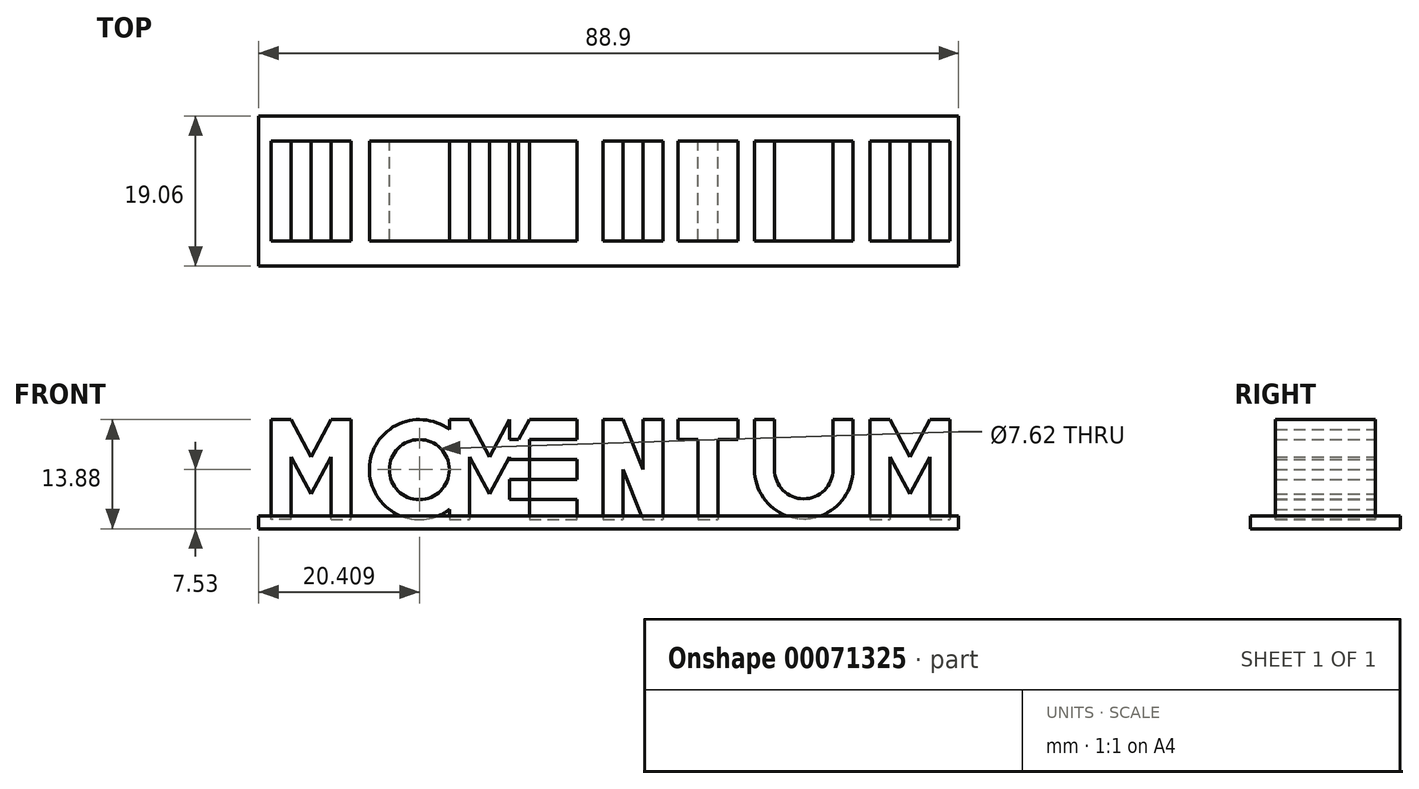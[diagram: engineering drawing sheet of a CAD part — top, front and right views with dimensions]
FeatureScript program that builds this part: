
annotation { "Feature Type Name" : "Feature", "Feature Type Description" : "" }
export const myFeature = defineFeature(function(context is Context, id is Id, definition is map)
    precondition{}
    {
        {
            var Q0;
            Q0=qCreatedBy(makeId("Front.planeOp"),FACE);
            var sketch = newSketch(context, id + "F0", { "sketchPlane" : qUnion([Q0])});
            skLineSegment(sketch, "E0.rect.bottom", {"start": v(-39.63, -6.35) * mm, "end": v(-42.17, -6.35) * mm});
            skLineSegment(sketch, "E0.rect.top", {"start": v(-39.63, 6.35) * mm, "end": v(-42.17, 6.35) * mm});
            skLineSegment(sketch, "E0.rect.left", {"start": v(-39.63, -6.35) * mm, "end": v(-39.63, 6.35) * mm});
            skLineSegment(sketch, "E0.rect.right", {"start": v(-42.17, -6.35) * mm, "end": v(-42.17, 6.35) * mm});
            skPoint(sketch, "E0.rect.middle", {"position": v(-40.9, 0) * mm});
            skLineSegment(sketch, "E1", {"start": v(-42.17, 6.35) * mm, "end": v(3.15, 6.35) * mm});
            skPoint(sketch, "E1.endSnap0", {"position": v(-40.9, 6.35) * mm});
            skLineSegment(sketch, "E2", {"start": v(-42.17, -6.35) * mm, "end": v(48.91, -6.35) * mm});
            skPoint(sketch, "E2.endSnap0", {"position": v(-40.9, -6.35) * mm});
            skLineSegment(sketch, "E3", {"start": v(-37.1, 6.35) * mm, "end": v(-37.1, -6.35) * mm});
            skLineSegment(sketch, "E4.MirrorCS", {"start": v(-34.55, -6.35) * mm, "end": v(-34.55, 6.35) * mm});
            skLineSegment(sketch, "E5.MirrorCS", {"start": v(-32.01, -6.35) * mm, "end": v(-32.01, 6.35) * mm});
            skLineSegment(sketch, "E6", {"start": v(-42.17, 6.35) * mm, "end": v(-37.1, -3.1) * mm});
            skLineSegment(sketch, "E7", {"start": v(-39.63, 6.35) * mm, "end": v(-37.1, 1.63) * mm});
            skLineSegment(sketch, "E8", {"start": v(-37.1, 1.63) * mm, "end": v(-34.55, 6.35) * mm});
            skLineSegment(sketch, "E9", {"start": v(-32.01, 6.35) * mm, "end": v(-37.1, -3.1) * mm});
            skCircle(sketch, "E10", {"center": v(-23.32, 0) * mm, "radius": 6.35 * mm});
            skCircle(sketch, "E11", {"center": v(-23.32, 0) * mm, "radius": 3.8 * mm});
            skLineSegment(sketch, "E12", {"start": v(-19.51, 0) * mm, "end": v(-16.97, 0) * mm});
            skLineSegment(sketch, "E13", {"start": v(-19.51, 6.35) * mm, "end": v(-19.51, -6.35) * mm});
            skLineSegment(sketch, "E14", {"start": v(-16.97, 6.35) * mm, "end": v(-16.97, -6.35) * mm});
            skLineSegment(sketch, "E15", {"start": v(-14.43, 6.35) * mm, "end": v(-14.43, -6.35) * mm});
            skLineSegment(sketch, "E16", {"start": v(-11.9, 6.35) * mm, "end": v(-11.9, -6.35) * mm});
            skLineSegment(sketch, "E17", {"start": v(-9.35, 6.35) * mm, "end": v(-9.35, -6.35) * mm});
            skLineSegment(sketch, "E18", {"start": v(-19.51, 6.35) * mm, "end": v(-14.43, -3.1) * mm});
            skLineSegment(sketch, "E19", {"start": v(-14.43, -3.1) * mm, "end": v(-9.35, 6.35) * mm});
            skLineSegment(sketch, "E20", {"start": v(-16.97, 6.35) * mm, "end": v(-14.43, 1.62) * mm});
            skLineSegment(sketch, "E21", {"start": v(-14.43, 1.62) * mm, "end": v(-11.9, 6.35) * mm});
            skLineSegment(sketch, "E22", {"start": v(3.15, 6.35) * mm, "end": v(48.32, 6.35) * mm});
            skLineSegment(sketch, "E23.bottom", {"start": v(-11.9, 6.35) * mm, "end": v(-3.3, 6.35) * mm});
            skLineSegment(sketch, "E23.top", {"start": v(-11.9, 3.81) * mm, "end": v(-3.3, 3.81) * mm});
            skLineSegment(sketch, "E23.left", {"start": v(-11.9, 6.35) * mm, "end": v(-11.9, 3.81) * mm});
            skLineSegment(sketch, "E23.right", {"start": v(-3.3, 6.35) * mm, "end": v(-3.3, 3.81) * mm});
            skLineSegment(sketch, "E24.bottom", {"start": v(-11.9, 1.27) * mm, "end": v(-3.3, 1.27) * mm});
            skLineSegment(sketch, "E24.top", {"start": v(-11.9, -1.27) * mm, "end": v(-3.3, -1.27) * mm});
            skLineSegment(sketch, "E24.left", {"start": v(-11.9, 1.27) * mm, "end": v(-11.9, -1.27) * mm});
            skLineSegment(sketch, "E24.right", {"start": v(-3.3, 1.27) * mm, "end": v(-3.3, -1.27) * mm});
            skLineSegment(sketch, "E25.bottom", {"start": v(-11.9, -6.35) * mm, "end": v(-3.3, -6.35) * mm});
            skLineSegment(sketch, "E25.top", {"start": v(-11.9, -3.8) * mm, "end": v(-3.3, -3.8) * mm});
            skLineSegment(sketch, "E25.left", {"start": v(-11.9, -6.35) * mm, "end": v(-11.9, -3.8) * mm});
            skLineSegment(sketch, "E25.right", {"start": v(-3.3, -6.35) * mm, "end": v(-3.3, -3.8) * mm});
            skLineSegment(sketch, "E26", {"start": v(0, 6.35) * mm, "end": v(0, -6.35) * mm});
            skLineSegment(sketch, "E27", {"start": v(2.54, 6.35) * mm, "end": v(2.54, -6.35) * mm});
            skLineSegment(sketch, "E28", {"start": v(5.08, 6.35) * mm, "end": v(5.08, -6.35) * mm});
            skLineSegment(sketch, "E29", {"start": v(7.62, 6.35) * mm, "end": v(7.62, -6.35) * mm});
            skLineSegment(sketch, "E30", {"start": v(0, 6.35) * mm, "end": v(5.08, -6.35) * mm});
            skLineSegment(sketch, "E31", {"start": v(2.54, 6.35) * mm, "end": v(7.62, -6.35) * mm});
            skLineSegment(sketch, "E32.bottom", {"start": v(12.07, 6.35) * mm, "end": v(14.6, 6.35) * mm});
            skLineSegment(sketch, "E32.top", {"start": v(12.07, -6.35) * mm, "end": v(14.6, -6.35) * mm});
            skLineSegment(sketch, "E32.left", {"start": v(12.07, 6.35) * mm, "end": v(12.07, -6.35) * mm});
            skLineSegment(sketch, "E32.right", {"start": v(14.6, 6.35) * mm, "end": v(14.6, -6.35) * mm});
            skLineSegment(sketch, "E33.bottom", {"start": v(9.53, 6.35) * mm, "end": v(17.15, 6.35) * mm});
            skLineSegment(sketch, "E33.top", {"start": v(9.53, 3.81) * mm, "end": v(17.15, 3.81) * mm});
            skLineSegment(sketch, "E33.left", {"start": v(9.53, 6.35) * mm, "end": v(9.53, 3.81) * mm});
            skLineSegment(sketch, "E33.right", {"start": v(17.15, 6.35) * mm, "end": v(17.15, 3.81) * mm});
            skArc(sketch, "E34", {"start": v(19.25, 0) * mm, "mid": v(25.5, -6.25) * mm, "end": v(31.76, 0) * mm});
            skArc(sketch, "E35", {"start": v(21.79, 0) * mm, "mid": v(25.5, -3.71) * mm, "end": v(29.22, 0) * mm});
            skLineSegment(sketch, "E36", {"start": v(19.25, 0) * mm, "end": v(19.25, 6.35) * mm});
            skLineSegment(sketch, "E37", {"start": v(21.79, 0) * mm, "end": v(21.79, 6.35) * mm});
            skLineSegment(sketch, "E38", {"start": v(29.22, 0) * mm, "end": v(29.22, 6.35) * mm});
            skLineSegment(sketch, "E39", {"start": v(31.76, 0) * mm, "end": v(31.76, 6.35) * mm});
            skLineSegment(sketch, "E40", {"start": v(33.92, 6.35) * mm, "end": v(33.92, -6.35) * mm});
            skLineSegment(sketch, "E41", {"start": v(36.46, 6.35) * mm, "end": v(36.46, -6.35) * mm});
            skLineSegment(sketch, "E42", {"start": v(39, 6.35) * mm, "end": v(39, -6.35) * mm});
            skLineSegment(sketch, "E43", {"start": v(41.54, 6.35) * mm, "end": v(41.54, -6.35) * mm});
            skLineSegment(sketch, "E44", {"start": v(44.08, 6.35) * mm, "end": v(44.08, -6.35) * mm});
            skLineSegment(sketch, "E45", {"start": v(33.92, 6.35) * mm, "end": v(39, -3.1) * mm});
            skLineSegment(sketch, "E46", {"start": v(39, -3.1) * mm, "end": v(44.08, 6.35) * mm});
            skLineSegment(sketch, "E47", {"start": v(36.46, 6.35) * mm, "end": v(39, 1.63) * mm});
            skLineSegment(sketch, "E48", {"start": v(39, 1.63) * mm, "end": v(41.54, 6.35) * mm});
            skSolve(sketch);
        }
        {
            var Q0;
            {var subQ5=sQuery(id+"F0.wireOp",EDGE,"E0.rect.right");Q0=makeQuery(id+"F0.imprint","IMPRINT",FACE,{"disambiguationData":[TD([[makeQuery(id+"F0.imprint","IMPRINT",EDGE,{"derivedFrom":subQ5}),-1.0]])]});}
            var Q1;
            {var subQ1=sQuery(id+"F0.wireOp",EDGE,"E0.rect.left");var subQ3=sQuery(id+"F0.wireOp",EDGE,"E6");var subQ4=makeQuery(id+"F0.imprint","INTERSECT",VERTEX,{"derivedFrom":[subQ1,subQ3]});Q1=makeQuery(id+"F0.imprint","IMPRINT",FACE,{"disambiguationData":[TD([[makeQuery(id+"F0.imprint","IMPRINT",EDGE,{"disambiguationData":[TD([[subQ4,-1.0]])],"derivedFrom":subQ1}),1.0]])]});}
            var Q2;
            {var subQ0=sQuery(id+"F0.wireOp",EDGE,"E7");Q2=makeQuery(id+"F0.imprint","IMPRINT",FACE,{"disambiguationData":[TD([[makeQuery(id+"F0.imprint","IMPRINT",EDGE,{"derivedFrom":subQ0}),-1.0]])]});}
            var Q3;
            {var subQ3=sQuery(id+"F0.wireOp",EDGE,"E8");Q3=makeQuery(id+"F0.imprint","IMPRINT",FACE,{"disambiguationData":[TD([[makeQuery(id+"F0.imprint","IMPRINT",EDGE,{"derivedFrom":subQ3}),-1.0]])]});}
            var Q4;
            {var subQ0=sQuery(id+"F0.wireOp",EDGE,"E4.MirrorCS");var subQ3=sQuery(id+"F0.wireOp",EDGE,"E9");var subQ5=makeQuery(id+"F0.imprint","INTERSECT",VERTEX,{"derivedFrom":[subQ0,subQ3]});Q4=makeQuery(id+"F0.imprint","IMPRINT",FACE,{"disambiguationData":[TD([[makeQuery(id+"F0.imprint","IMPRINT",EDGE,{"disambiguationData":[TD([[subQ5,-1.0]])],"derivedFrom":subQ0}),-1.0]])]});}
            var Q5;
            {var subQ3=sQuery(id+"F0.wireOp",EDGE,"E5.MirrorCS");Q5=makeQuery(id+"F0.imprint","IMPRINT",FACE,{"disambiguationData":[TD([[makeQuery(id+"F0.imprint","IMPRINT",EDGE,{"derivedFrom":subQ3}),1.0]])]});}
            var Q6;
            {var subQ0=sQuery(id+"F0.wireOp",EDGE,"E11");Q6=makeQuery(id+"F0.imprint","IMPRINT",FACE,{"disambiguationData":[TD([[makeQuery(id+"F0.imprint","IMPRINT",EDGE,{"derivedFrom":subQ0}),-1.0]])]});}
            var Q7;
            {var subQ0=sQuery(id+"F0.wireOp",EDGE,"E12");Q7=makeQuery(id+"F0.imprint","IMPRINT",FACE,{"disambiguationData":[TD([[makeQuery(id+"F0.imprint","IMPRINT",EDGE,{"derivedFrom":subQ0}),1.0]])]});}
            var Q8;
            {var subQ0=sQuery(id+"F0.wireOp",EDGE,"E12");Q8=makeQuery(id+"F0.imprint","IMPRINT",FACE,{"disambiguationData":[TD([[makeQuery(id+"F0.imprint","IMPRINT",EDGE,{"derivedFrom":subQ0}),-1.0]])]});}
            var Q9;
            {var subQ0=sQuery(id+"F0.wireOp",EDGE,"E13");var subQ1=sQuery(id+"F0.wireOp",EDGE,"E2");var subQ2=makeQuery(id+"F0.imprint","INTERSECT",VERTEX,{"derivedFrom":[subQ1,subQ0]});Q9=makeQuery(id+"F0.imprint","IMPRINT",FACE,{"disambiguationData":[TD([[makeQuery(id+"F0.imprint","IMPRINT",EDGE,{"disambiguationData":[TD([[subQ2,-1.0]])],"derivedFrom":subQ1}),1.0]])]});}
            var Q10;
            {var subQ0=sQuery(id+"F0.wireOp",EDGE,"E18");var subQ3=sQuery(id+"F0.wireOp",EDGE,"E14");var subQ5=makeQuery(id+"F0.imprint","INTERSECT",VERTEX,{"derivedFrom":[subQ3,subQ0]});Q10=makeQuery(id+"F0.imprint","IMPRINT",FACE,{"disambiguationData":[TD([[makeQuery(id+"F0.imprint","IMPRINT",EDGE,{"disambiguationData":[TD([[subQ5,1.0]])],"derivedFrom":subQ3}),-1.0]])]});}
            var Q11;
            {var subQ1=sQuery(id+"F0.wireOp",EDGE,"E10");var subQ3=sQuery(id+"F0.wireOp",EDGE,"E13");var subQ4=makeQuery(id+"F0.imprint","INTERSECT",VERTEX,{"disambiguationData":[OD(0.0)],"derivedFrom":[subQ1,subQ3]});Q11=makeQuery(id+"F0.imprint","IMPRINT",FACE,{"disambiguationData":[TD([[makeQuery(id+"F0.imprint","IMPRINT",EDGE,{"disambiguationData":[TD([[subQ4,1.0]])],"derivedFrom":subQ1}),-1.0]])]});}
            var Q12;
            {var subQ0=sQuery(id+"F0.wireOp",EDGE,"E20");Q12=makeQuery(id+"F0.imprint","IMPRINT",FACE,{"disambiguationData":[TD([[makeQuery(id+"F0.imprint","IMPRINT",EDGE,{"derivedFrom":subQ0}),-1.0]])]});}
            var Q13;
            {var subQ5=sQuery(id+"F0.wireOp",EDGE,"E21");Q13=makeQuery(id+"F0.imprint","IMPRINT",FACE,{"disambiguationData":[TD([[makeQuery(id+"F0.imprint","IMPRINT",EDGE,{"derivedFrom":subQ5}),-1.0]])]});}
            var Q14;
            {var subQ5=sQuery(id+"F0.wireOp",EDGE,"E23.left");Q14=makeQuery(id+"F0.imprint","IMPRINT",FACE,{"disambiguationData":[TD([[makeQuery(id+"F0.imprint","IMPRINT",EDGE,{"derivedFrom":subQ5}),1.0]])]});}
            var Q15;
            {var subQ1=sQuery(id+"F0.wireOp",EDGE,"E16");var subQ3=sQuery(id+"F0.wireOp",EDGE,"E19");var subQ4=makeQuery(id+"F0.imprint","INTERSECT",VERTEX,{"derivedFrom":[subQ1,subQ3]});Q15=makeQuery(id+"F0.imprint","IMPRINT",FACE,{"disambiguationData":[TD([[makeQuery(id+"F0.imprint","IMPRINT",EDGE,{"disambiguationData":[TD([[subQ4,-1.0]])],"derivedFrom":subQ3}),1.0]])]});}
            var Q16;
            {var subQ5=sQuery(id+"F0.wireOp",EDGE,"E23.right");Q16=makeQuery(id+"F0.imprint","IMPRINT",FACE,{"disambiguationData":[TD([[makeQuery(id+"F0.imprint","IMPRINT",EDGE,{"derivedFrom":subQ5}),-1.0]])]});}
            var Q17;
            {var subQ0=sQuery(id+"F0.wireOp",EDGE,"E23.top");var subQ1=sQuery(id+"F0.wireOp",EDGE,"E17");var subQ2=makeQuery(id+"F0.imprint","INTERSECT",VERTEX,{"derivedFrom":[subQ1,subQ0]});Q17=makeQuery(id+"F0.imprint","IMPRINT",FACE,{"disambiguationData":[TD([[makeQuery(id+"F0.imprint","IMPRINT",EDGE,{"disambiguationData":[TD([[subQ2,-1.0]])],"derivedFrom":subQ1}),-1.0]])]});}
            var Q18;
            {var subQ1=sQuery(id+"F0.wireOp",EDGE,"E17");var subQ3=sQuery(id+"F0.wireOp",EDGE,"E23.top");var subQ4=makeQuery(id+"F0.imprint","INTERSECT",VERTEX,{"derivedFrom":[subQ1,subQ3]});Q18=makeQuery(id+"F0.imprint","IMPRINT",FACE,{"disambiguationData":[TD([[makeQuery(id+"F0.imprint","IMPRINT",EDGE,{"disambiguationData":[TD([[subQ4,1.0]])],"derivedFrom":subQ3}),1.0]])]});}
            var Q19;
            {var subQ5=sQuery(id+"F0.wireOp",EDGE,"E24.left");Q19=makeQuery(id+"F0.imprint","IMPRINT",FACE,{"disambiguationData":[TD([[makeQuery(id+"F0.imprint","IMPRINT",EDGE,{"derivedFrom":subQ5}),1.0]])]});}
            var Q20;
            {var subQ5=sQuery(id+"F0.wireOp",EDGE,"E24.right");Q20=makeQuery(id+"F0.imprint","IMPRINT",FACE,{"disambiguationData":[TD([[makeQuery(id+"F0.imprint","IMPRINT",EDGE,{"derivedFrom":subQ5}),-1.0]])]});}
            var Q21;
            {var subQ3=sQuery(id+"F0.wireOp",EDGE,"E24.top");var subQ5=sQuery(id+"F0.wireOp",EDGE,"E17");var subQ6=makeQuery(id+"F0.imprint","INTERSECT",VERTEX,{"derivedFrom":[subQ5,subQ3]});Q21=makeQuery(id+"F0.imprint","IMPRINT",FACE,{"disambiguationData":[TD([[makeQuery(id+"F0.imprint","IMPRINT",EDGE,{"disambiguationData":[TD([[subQ6,-1.0]])],"derivedFrom":subQ5}),-1.0]])]});}
            var Q22;
            {var subQ5=sQuery(id+"F0.wireOp",EDGE,"E25.left");Q22=makeQuery(id+"F0.imprint","IMPRINT",FACE,{"disambiguationData":[TD([[makeQuery(id+"F0.imprint","IMPRINT",EDGE,{"derivedFrom":subQ5}),-1.0]])]});}
            var Q23;
            {var subQ5=sQuery(id+"F0.wireOp",EDGE,"E25.right");Q23=makeQuery(id+"F0.imprint","IMPRINT",FACE,{"disambiguationData":[TD([[makeQuery(id+"F0.imprint","IMPRINT",EDGE,{"derivedFrom":subQ5}),1.0]])]});}
            var Q24;
            {var subQ0=sQuery(id+"F0.wireOp",EDGE,"E26");Q24=makeQuery(id+"F0.imprint","IMPRINT",FACE,{"disambiguationData":[TD([[makeQuery(id+"F0.imprint","IMPRINT",EDGE,{"derivedFrom":subQ0}),1.0]])]});}
            var Q25;
            {var subQ0=sQuery(id+"F0.wireOp",EDGE,"E30");var subQ3=sQuery(id+"F0.wireOp",EDGE,"E27");var subQ5=makeQuery(id+"F0.imprint","INTERSECT",VERTEX,{"derivedFrom":[subQ3,subQ0]});Q25=makeQuery(id+"F0.imprint","IMPRINT",FACE,{"disambiguationData":[TD([[makeQuery(id+"F0.imprint","IMPRINT",EDGE,{"disambiguationData":[TD([[subQ5,1.0]])],"derivedFrom":subQ3}),-1.0]])]});}
            var Q26;
            {var subQ1=sQuery(id+"F0.wireOp",EDGE,"E27");var subQ3=sQuery(id+"F0.wireOp",EDGE,"E30");var subQ4=makeQuery(id+"F0.imprint","INTERSECT",VERTEX,{"derivedFrom":[subQ1,subQ3]});Q26=makeQuery(id+"F0.imprint","IMPRINT",FACE,{"disambiguationData":[TD([[makeQuery(id+"F0.imprint","IMPRINT",EDGE,{"disambiguationData":[TD([[subQ4,1.0]])],"derivedFrom":subQ1}),1.0]])]});}
            var Q27;
            {var subQ0=sQuery(id+"F0.wireOp",EDGE,"E28");var subQ3=sQuery(id+"F0.wireOp",EDGE,"E31");var subQ5=makeQuery(id+"F0.imprint","INTERSECT",VERTEX,{"derivedFrom":[subQ0,subQ3]});Q27=makeQuery(id+"F0.imprint","IMPRINT",FACE,{"disambiguationData":[TD([[makeQuery(id+"F0.imprint","IMPRINT",EDGE,{"disambiguationData":[TD([[subQ5,-1.0]])],"derivedFrom":subQ0}),1.0]])]});}
            var Q28;
            {var subQ3=sQuery(id+"F0.wireOp",EDGE,"E29");Q28=makeQuery(id+"F0.imprint","IMPRINT",FACE,{"disambiguationData":[TD([[makeQuery(id+"F0.imprint","IMPRINT",EDGE,{"derivedFrom":subQ3}),-1.0]])]});}
            var Q29;
            {var subQ0=sQuery(id+"F0.wireOp",EDGE,"E32.top");Q29=makeQuery(id+"F0.imprint","IMPRINT",FACE,{"disambiguationData":[TD([[makeQuery(id+"F0.imprint","IMPRINT",EDGE,{"derivedFrom":subQ0}),1.0]])]});}
            var Q30;
            {var subQ5=sQuery(id+"F0.wireOp",EDGE,"E33.right");Q30=makeQuery(id+"F0.imprint","IMPRINT",FACE,{"disambiguationData":[TD([[makeQuery(id+"F0.imprint","IMPRINT",EDGE,{"derivedFrom":subQ5}),-1.0]])]});}
            var Q31;
            {var subQ0=sQuery(id+"F0.wireOp",EDGE,"E33.bottom");var subQ1=sQuery(id+"F0.wireOp",EDGE,"E32.left");var subQ2=makeQuery(id+"F0.imprint","INTERSECT",VERTEX,{"derivedFrom":[subQ1,subQ0]});Q31=makeQuery(id+"F0.imprint","IMPRINT",FACE,{"disambiguationData":[TD([[makeQuery(id+"F0.imprint","IMPRINT",EDGE,{"disambiguationData":[TD([[subQ2,-1.0]])],"derivedFrom":subQ1}),1.0]])]});}
            var Q32;
            {var subQ5=sQuery(id+"F0.wireOp",EDGE,"E33.left");Q32=makeQuery(id+"F0.imprint","IMPRINT",FACE,{"disambiguationData":[TD([[makeQuery(id+"F0.imprint","IMPRINT",EDGE,{"derivedFrom":subQ5}),1.0]])]});}
            var Q33;
            Q33=makeQuery(id+"F0.imprint","IMPRINT",FACE,{"disambiguationData":[TD([[makeQuery(id+"F0.imprint","IMPRINT",EDGE,{"derivedFrom":sQuery(id+"F0.wireOp",EDGE,"E34")}),1.0]])]});
            var Q34;
            {var subQ0=sQuery(id+"F0.wireOp",EDGE,"E40");Q34=makeQuery(id+"F0.imprint","IMPRINT",FACE,{"disambiguationData":[TD([[makeQuery(id+"F0.imprint","IMPRINT",EDGE,{"derivedFrom":subQ0}),1.0]])]});}
            var Q35;
            {var subQ0=sQuery(id+"F0.wireOp",EDGE,"E45");var subQ3=sQuery(id+"F0.wireOp",EDGE,"E41");var subQ5=makeQuery(id+"F0.imprint","INTERSECT",VERTEX,{"derivedFrom":[subQ3,subQ0]});Q35=makeQuery(id+"F0.imprint","IMPRINT",FACE,{"disambiguationData":[TD([[makeQuery(id+"F0.imprint","IMPRINT",EDGE,{"disambiguationData":[TD([[subQ5,1.0]])],"derivedFrom":subQ3}),-1.0]])]});}
            var Q36;
            {var subQ0=sQuery(id+"F0.wireOp",EDGE,"E47");Q36=makeQuery(id+"F0.imprint","IMPRINT",FACE,{"disambiguationData":[TD([[makeQuery(id+"F0.imprint","IMPRINT",EDGE,{"derivedFrom":subQ0}),-1.0]])]});}
            var Q37;
            {var subQ3=sQuery(id+"F0.wireOp",EDGE,"E48");Q37=makeQuery(id+"F0.imprint","IMPRINT",FACE,{"disambiguationData":[TD([[makeQuery(id+"F0.imprint","IMPRINT",EDGE,{"derivedFrom":subQ3}),-1.0]])]});}
            var Q38;
            {var subQ0=sQuery(id+"F0.wireOp",EDGE,"E43");var subQ3=sQuery(id+"F0.wireOp",EDGE,"E46");var subQ5=makeQuery(id+"F0.imprint","INTERSECT",VERTEX,{"derivedFrom":[subQ0,subQ3]});Q38=makeQuery(id+"F0.imprint","IMPRINT",FACE,{"disambiguationData":[TD([[makeQuery(id+"F0.imprint","IMPRINT",EDGE,{"disambiguationData":[TD([[subQ5,1.0]])],"derivedFrom":subQ0}),1.0]])]});}
            var Q39;
            {var subQ3=sQuery(id+"F0.wireOp",EDGE,"E44");Q39=makeQuery(id+"F0.imprint","IMPRINT",FACE,{"disambiguationData":[TD([[makeQuery(id+"F0.imprint","IMPRINT",EDGE,{"derivedFrom":subQ3}),-1.0]])]});}
            extrude(context, id + "F1", {"entities" : qUnion([Q0, Q1, Q2, Q3, Q4, Q5, Q6, Q7, Q8, Q9, Q10, Q11, Q12, Q13, Q14, Q15, Q16, Q17, Q18, Q19, Q20, Q21, Q22, Q23, Q24, Q25, Q26, Q27, Q28, Q29, Q30, Q31, Q32, Q33, Q34, Q35, Q36, Q37, Q38, Q39]), "endBound" : BoundingType.SYMMETRIC, "depth" : 12.7 * mm});
        }
        {
            var Q0;
            Q0=qCreatedBy(makeId("Front.planeOp"),FACE);
            var sketch = newSketch(context, id + "F2", { "sketchPlane" : qUnion([Q0])});
            skLineSegment(sketch, "E49.bottom", {"start": v(-43.73, -5.87) * mm, "end": v(45.17, -5.87) * mm});
            skLineSegment(sketch, "E49.top", {"start": v(-43.73, -7.53) * mm, "end": v(45.17, -7.53) * mm});
            skLineSegment(sketch, "E49.left", {"start": v(-43.73, -5.87) * mm, "end": v(-43.73, -7.53) * mm});
            skLineSegment(sketch, "E49.right", {"start": v(45.17, -5.87) * mm, "end": v(45.17, -7.53) * mm});
            skSolve(sketch);
        }
        {
            var Q0;
            Q0=makeQuery(id+"F2.imprint","IMPRINT",FACE,{"disambiguationData":[TD([[makeQuery(id+"F2.imprint","IMPRINT",EDGE,{"derivedFrom":sQuery(id+"F2.wireOp",EDGE,"E49.bottom")}),-1.0]])]});
            extrude(context, id + "F3", {"entities" : qUnion([Q0]), "endBound" : BoundingType.SYMMETRIC, "depth" : 19.05 * mm});
        }
    });
